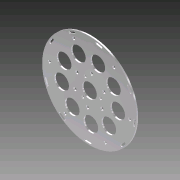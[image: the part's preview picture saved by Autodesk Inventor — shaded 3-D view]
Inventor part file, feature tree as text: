
AUTODESK INVENTOR PART (.ipt)
format: ipt  version: 2011 (Build 150239000, 239)  size: 254,976 bytes
history: native  units: in
note: dims shown in document units (in); Inventor stores cm internally (conversion verified against a paired STEP export)
features: extrude x1, sketch x1
ambient origin geometry x8: Origin, YZ Plane, XZ Plane, XY Plane, X Axis, Y Axis, Z Axis, Center Point
bodies: Solid1 (feature_tree)
feature tree (2):
  extrude  "Extrusion1"  Depth=0.0875in TaperAngle=0.0deg
  sketch  "Sketch1"  dims[d1=1.1811in d3=2.3622in d5=3.5433in d7=2.3622in d9=0.7874in d11=0.7874in d13=0.7874in d15=1.1811in d17=0.7874in d19=1.1811in d20=5.657in d21=0.875in d22=0.16in d23=0.145in d24=360.0deg d25=0.192in d26=0.319in d27=0.406in d28=360.0deg d29=0.875in d30=0.525in d31=360.0deg d32=0.1705in d33=0.19in d34=360.0deg d35=0.103in d36=0.19in d37=0.2405in d38=0.2405in d39=0.3436in d40=0.481in d41=0.3436in d42=0.481in d43=0.0875in d44=0.0in]
